# Revit family: WB6-27
name_source: partatom
category: Attrezzature speciali
revit_build: Autodesk Revit 2014 (Build: 20130308_1515(x64)
units: mm (PartAtom-declared; Revit-internal decimal feet)

## types (1)
- WB6-27
    Cold Water Connection Height = 0 mm  [stored 0 ft]
    Cold Water Maximum Pressure = 0.00 psi
    Cold Water Minimum Pressure = 0.00 psi
    Cold Water Size = 1"
    Conn Conduit = Sì
    Descrizione = EL.BAINM,11GN,TAP(B),1S,BS,400X900X250H
    Electrical Remarks = 400 V/3N ph/50/60 Hz
    Hot Water Connection Height = 0 mm  [stored 0 ft]
    Hot Water Consumption = 0 GPM
    Hot Water Maximum Pressure = 0.00 psi
    Hot Water Minimum Pressure = 0.00 psi
    Hot Water Size = 1"
    Hot Water Temperature = -460 °F
    Indirect Waste Connection Height = 0 mm  [stored 0 ft]
    Indirect Waste Size = 1"
    Max Overcurrent Protection = 0 A
    Min Ckt Ampacity = 0 A
    Modello = 589133
    Phase = 3
    Produttore = ELECTROLUX
    Volts = 400 V
    Watts = 1500 W
    Weight in Pounds = 55.1

note: [stored X ft] marks values corroborated as IEEE doubles in the binary element streams (Revit-internal decimal feet)

## geometry (parser evidence)
native form markers: Blend x12, Sweep x3
no freeform markers — native parametric forms only
